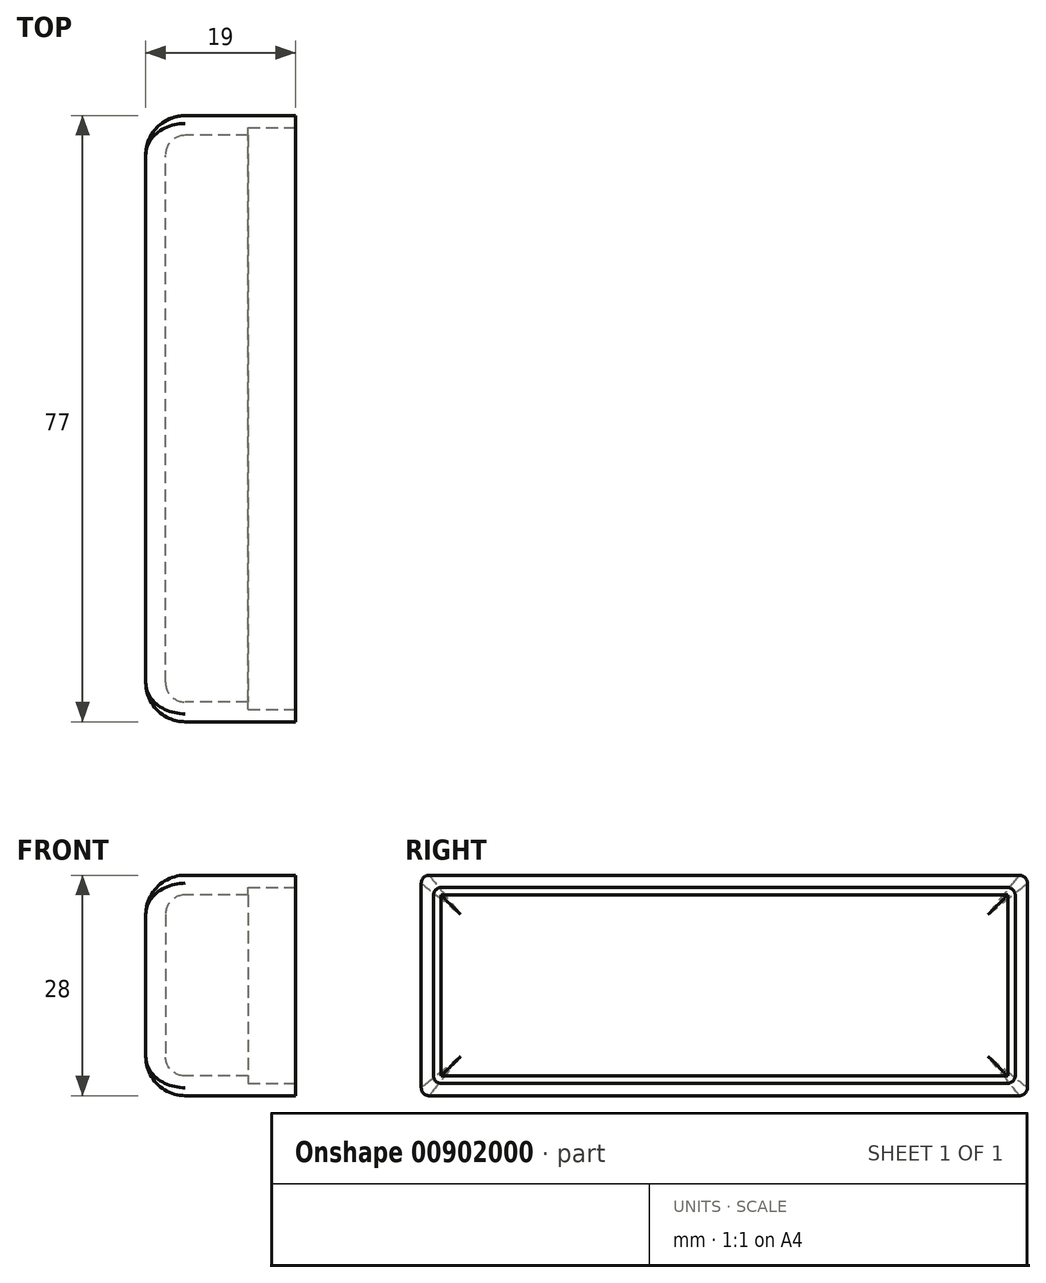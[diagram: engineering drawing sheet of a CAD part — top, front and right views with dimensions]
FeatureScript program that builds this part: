
annotation { "Feature Type Name" : "Feature", "Feature Type Description" : "" }
export const myFeature = defineFeature(function(context is Context, id is Id, definition is map)
    precondition{}
    {
        {
            var Q0;
            Q0=qCreatedBy(makeId("Top.planeOp"),FACE);
            var sketch = newSketch(context, id + "F0", { "sketchPlane" : qUnion([Q0])});
            skLineSegment(sketch, "E0.bottom", {"start": v(-9.5, 38.5) * mm, "end": v(9.5, 38.5) * mm});
            skLineSegment(sketch, "E0.top", {"start": v(-9.5, -38.5) * mm, "end": v(9.5, -38.5) * mm});
            skLineSegment(sketch, "E0.left", {"start": v(-9.5, 38.5) * mm, "end": v(-9.5, -38.5) * mm});
            skLineSegment(sketch, "E0.right", {"start": v(9.5, 38.5) * mm, "end": v(9.5, -38.5) * mm});
            skPoint(sketch, "E0.middle", {"position": v(0, 0) * mm});
            skSolve(sketch);
        }
        {
            var Q0;
            Q0=qSketchRegion(id+"F0",true);
            extrude(context, id + "F1", {"entities" : qUnion([Q0]), "endBound" : BoundingType.SYMMETRIC, "depth" : 28 * mm, "offsetDistance" : 25 * mm});
        }
        {
            var Q0;
            {var subQ0=sQuery(id+"F0.wireOp",EDGE,"E0.bottom");Q0=makeQuery(id+"F4.opShell","OFFSET_EDGE",EDGE,{"disambiguationData":[OSD([subQ0]),TDD([makeQuery(id+"F1.opExtrude","CAP_EDGE",EDGE,{"disambiguationData":[OSD([subQ0])],"isStart":false})])]});}
            var Q1;
            Q1=makeQuery(id+"F1.opExtrude","CAP_EDGE",EDGE,{"disambiguationData":[OSD([sQuery(id+"F0.wireOp",EDGE,"E0.top")])],"isStart":false});
            var Q2;
            Q2=makeQuery(id+"F1.opExtrude","CAP_EDGE",EDGE,{"disambiguationData":[OSD([sQuery(id+"F0.wireOp",EDGE,"E0.top")])],"isStart":true});
            var Q3;
            Q3=makeQuery(id+"F1.opExtrude","CAP_EDGE",EDGE,{"disambiguationData":[OSD([sQuery(id+"F0.wireOp",EDGE,"E0.bottom")])],"isStart":true});
            var Q4;
            Q4=makeQuery(id+"F1.opExtrude","CAP_EDGE",EDGE,{"disambiguationData":[OSD([sQuery(id+"F0.wireOp",EDGE,"E0.bottom")])],"isStart":false});
            fillet(context, id + "F2", {"entities" : qUnion([Q0, Q1, Q2, Q3, Q4]), "radius" : 1 * mm, "tangentPropagation" : true, "allowEdgeOverflow" : false});
        }
        {
            var Q0;
            Q0=makeQuery(id+"F1.opExtrude","SWEPT_FACE",FACE,{"disambiguationData":[OSD([sQuery(id+"F0.wireOp",EDGE,"E0.left")])]});
            fillet(context, id + "F3", {"entities" : qUnion([Q0]), "radius" : 5 * mm, "tangentPropagation" : true, "allowEdgeOverflow" : false});
        }
        {
            var Q0;
            Q0=makeQuery(id+"F1.opExtrude","SWEPT_FACE",FACE,{"disambiguationData":[OSD([sQuery(id+"F0.wireOp",EDGE,"E0.right")])]});
            shell(context, id + "F4", {"entities" : qUnion([Q0]), "thickness" : 2.5 * mm});
        }
        {
            var Q0;
            Q0=makeQuery(id+"F1.opExtrude","SWEPT_FACE",FACE,{"disambiguationData":[OSD([sQuery(id+"F0.wireOp",EDGE,"E0.right")])]});
            var sketch = newSketch(context, id + "F5", { "sketchPlane" : qUnion([Q0])});
            skLineSegment(sketch, "E1.bottom", {"start": v(-36, 11.5) * mm, "end": v(36, 11.5) * mm});
            skLineSegment(sketch, "E1.top", {"start": v(-36, -11.5) * mm, "end": v(36, -11.5) * mm});
            skLineSegment(sketch, "E1.left", {"start": v(-36, 11.5) * mm, "end": v(-36, -11.5) * mm});
            skLineSegment(sketch, "E1.right", {"start": v(36, 11.5) * mm, "end": v(36, -11.5) * mm});
            skPoint(sketch, "E1.middle", {"position": v(0, 0) * mm});
            skLineSegment(sketch, "E2.0", {"start": v(-36.95, 12.45) * mm, "end": v(36.95, 12.45) * mm});
            skLineSegment(sketch, "E2.1", {"start": v(-36.95, 12.45) * mm, "end": v(-36.95, -12.45) * mm});
            skLineSegment(sketch, "E2.2", {"start": v(-36.95, -12.45) * mm, "end": v(36.95, -12.45) * mm});
            skLineSegment(sketch, "E2.3", {"start": v(36.95, 12.45) * mm, "end": v(36.95, -12.45) * mm});
            skSolve(sketch);
        }
        {
            var Q0;
            Q0 = qSketchRegion(id + "F5", true);
            extrude(context, id + "F6", {"entities" : qUnion([Q0]), "operationType" : NewBodyOperationType.REMOVE, "oppositeDirection" : true, "depth" : 6 * mm, "offsetDistance" : 25 * mm});
        }
        {
            var Q0;
            Q0=makeQuery(id+"F6.boolean.opBoolean","COPY",EDGE,{"derivedFrom":makeQuery(id+"F6.opExtrude","SWEPT_EDGE",EDGE,{"disambiguationData":[OSD([sQuery(id+"F5.wireOp",EDGE,"E2.0"),sQuery(id+"F5.wireOp",EDGE,"E2.1")])]})});
            var Q1;
            Q1=makeQuery(id+"F6.boolean.opBoolean","COPY",EDGE,{"derivedFrom":makeQuery(id+"F6.opExtrude","SWEPT_EDGE",EDGE,{"disambiguationData":[OSD([sQuery(id+"F5.wireOp",EDGE,"E2.0"),sQuery(id+"F5.wireOp",EDGE,"E2.3")])]})});
            var Q2;
            Q2=makeQuery(id+"F6.boolean.opBoolean","COPY",EDGE,{"derivedFrom":makeQuery(id+"F6.opExtrude","SWEPT_EDGE",EDGE,{"disambiguationData":[OSD([sQuery(id+"F5.wireOp",EDGE,"E2.2"),sQuery(id+"F5.wireOp",EDGE,"E2.3")])]})});
            var Q3;
            Q3=makeQuery(id+"F6.boolean.opBoolean","COPY",EDGE,{"derivedFrom":makeQuery(id+"F6.opExtrude","SWEPT_EDGE",EDGE,{"disambiguationData":[OSD([sQuery(id+"F5.wireOp",EDGE,"E2.1"),sQuery(id+"F5.wireOp",EDGE,"E2.2")])]})});
            fillet(context, id + "F7", {"entities" : qUnion([Q0, Q1, Q2, Q3]), "radius" : 1 * mm, "tangentPropagation" : true, "allowEdgeOverflow" : false});
        }
    });
